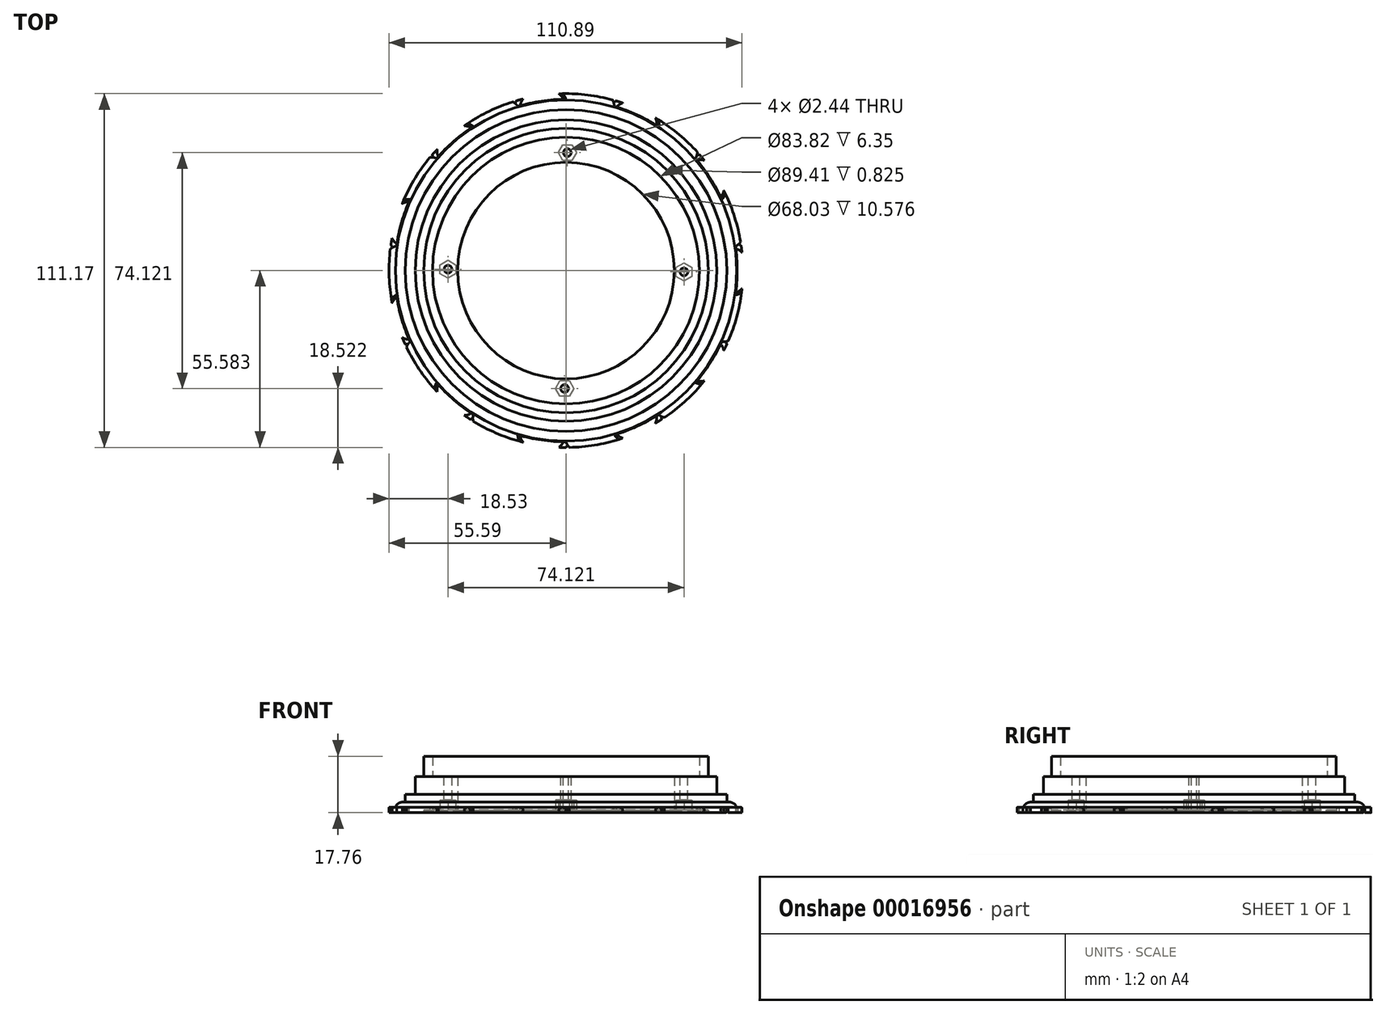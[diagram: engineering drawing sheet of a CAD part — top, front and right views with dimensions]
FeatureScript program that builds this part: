
annotation { "Feature Type Name" : "Feature", "Feature Type Description" : "" }
export const myFeature = defineFeature(function(context is Context, id is Id, definition is map)
    precondition{}
    {
        {
            var Q0;
            Q0=qCreatedBy(makeId("Top.planeOp"),FACE);
            var sketch = newSketch(context, id + "F0", { "sketchPlane" : qUnion([Q0])});
            skCircle(sketch, "E0", {"center": v(0, 0) * mm, "radius": 57.15 * mm, "construction": true});
            skLineSegment(sketch, "E1", {"start": v(0, 0) * mm, "end": v(0, 57.15) * mm, "construction": true});
            skCircle(sketch, "E2", {"center": v(0, 3.34) * mm, "radius": 53.8 * mm});
            skCircle(sketch, "E3", {"center": v(0, 3.34) * mm, "radius": 3.34 * mm, "construction": true});
            skLineSegment(sketch, "E4", {"start": v(0, 3.34) * mm, "end": v(-29.1, 48.6) * mm, "construction": true});
            skLineSegment(sketch, "E5", {"start": v(0, 57.15) * mm, "end": v(-29.1, 48.6) * mm, "construction": true});
            skLineSegment(sketch, "E6", {"start": v(-14.55, 52.88) * mm, "end": v(-29.1, 48.6) * mm, "construction": true});
            skLineSegment(sketch, "E7", {"start": v(-14.02, 24.18) * mm, "end": v(-21.82, 50.74) * mm, "construction": true});
            skCircle(sketch, "E8", {"center": v(-14.55, 52.88) * mm, "radius": 7.58 * mm, "construction": true});
            skLineSegment(sketch, "E9", {"start": v(-15.16, 54.97) * mm, "end": v(-16.68, 60.15) * mm, "construction": true});
            skEllipticalArc(sketch, "E10", {});
            skPoint(sketch, "E11", {"position": v(-15.16, 54.97) * mm});
            skLineSegment(sketch, "E12", {"start": v(-15.16, 54.97) * mm, "end": v(0, 54.97) * mm, "construction": true});
            skPoint(sketch, "E13", {"position": v(-7.58, 54.97) * mm});
            skCircle(sketch, "E14", {"center": v(0, 54.97) * mm, "radius": 7.58 * mm, "construction": true});
            skPoint(sketch, "E15", {"position": v(0, 62.55) * mm});
            skEllipticalArc(sketch, "E16", {});
            skCircle(sketch, "E17", {"center": v(0, 3.34) * mm, "radius": 44.7 * mm});
            skEllipticalArc(sketch, "E18.trimOffspring", {});
            skEllipticalArc(sketch, "E19.trimOffspring", {});
            skLineSegment(sketch, "E20", {"start": v(0, 3.34) * mm, "end": v(-8.33, 61.3) * mm, "construction": true});
            skCircle(sketch, "E21", {"center": v(0, 3.34) * mm, "radius": 55.59 * mm});
            skCircle(sketch, "E22", {"center": v(0, 3.34) * mm, "radius": 127 * mm});
            skLineSegment(sketch, "E23", {"start": v(0, 3.34) * mm, "end": v(-127, 3.34) * mm, "construction": true});
            skLineSegment(sketch, "E24", {"start": v(-53.8, 3.34) * mm, "end": v(-55.59, 3.34) * mm, "construction": true});
            skFitSpline(sketch, "E25.0", {"points": [v(-14.94, 56.45) * mm, v(-15.23, 54.97) * mm, v(-14.94, 53.49) * mm, v(-14.22, 52.3) * mm, v(-13.38, 51.41) * mm, v(-12.35, 50.56) * mm, v(-10.78, 49.6) * mm, v(-8.86, 48.81) * mm, v(-7.15, 48.3) * mm, v(-5.35, 47.87) * mm, v(-3.45, 47.59) * mm, v(-1.5, 47.44) * mm, v(0, 47.4) * mm, v(1.5, 47.44) * mm, v(3.45, 47.59) * mm, v(5.35, 47.87) * mm, v(7.15, 48.3) * mm, v(8.86, 48.81) * mm, v(10.78, 49.6) * mm, v(12.35, 50.56) * mm, v(13.38, 51.41) * mm, v(14.22, 52.3) * mm, v(14.94, 53.49) * mm, v(15.23, 54.97) * mm, v(14.94, 56.45) * mm, v(14.22, 57.63) * mm, v(13.38, 58.53) * mm, v(12.35, 59.38) * mm, v(10.78, 60.34) * mm, v(8.86, 61.13) * mm, v(7.15, 61.64) * mm, v(5.35, 62.07) * mm, v(3.45, 62.35) * mm, v(1.5, 62.5) * mm, v(0, 62.54) * mm, v(-1.5, 62.5) * mm, v(-3.45, 62.35) * mm, v(-5.35, 62.07) * mm, v(-7.15, 61.64) * mm, v(-8.86, 61.13) * mm, v(-10.78, 60.34) * mm, v(-12.35, 59.38) * mm, v(-13.38, 58.53) * mm, v(-14.22, 57.63) * mm, v(-14.94, 56.45) * mm, v(-15.23, 54.97) * mm, v(-14.94, 53.49) * mm]});
            skFitSpline(sketch, "E25.1", {"points": [v(0.2, 55.67) * mm, v(0.07, 57.17) * mm, v(-0.63, 58.5) * mm, v(-1.65, 59.44) * mm, v(-2.71, 60.06) * mm, v(-3.94, 60.6) * mm, v(-5.72, 61.07) * mm, v(-7.78, 61.28) * mm, v(-9.57, 61.3) * mm, v(-11.4, 61.2) * mm, v(-13.31, 60.94) * mm, v(-15.23, 60.52) * mm, v(-16.68, 60.14) * mm, v(-18.1, 59.68) * mm, v(-19.94, 59) * mm, v(-21.68, 58.18) * mm, v(-23.28, 57.27) * mm, v(-24.78, 56.3) * mm, v(-26.4, 55) * mm, v(-27.64, 53.63) * mm, v(-28.38, 52.53) * mm, v(-28.94, 51.43) * mm, v(-29.3, 50.1) * mm, v(-29.16, 48.59) * mm, v(-28.46, 47.25) * mm, v(-27.44, 46.32) * mm, v(-26.38, 45.7) * mm, v(-25.15, 45.17) * mm, v(-23.37, 44.69) * mm, v(-21.31, 44.47) * mm, v(-19.52, 44.46) * mm, v(-17.68, 44.56) * mm, v(-15.78, 44.82) * mm, v(-13.86, 45.23) * mm, v(-12.41, 45.62) * mm, v(-11, 46.08) * mm, v(-9.15, 46.77) * mm, v(-7.41, 47.58) * mm, v(-5.8, 48.5) * mm, v(-4.3, 49.47) * mm, v(-2.7, 50.76) * mm, v(-1.45, 52.12) * mm, v(-0.7, 53.23) * mm, v(-0.15, 54.33) * mm, v(0.2, 55.67) * mm, v(0.07, 57.17) * mm, v(-0.63, 58.5) * mm]});
            skLineSegment(sketch, "E26", {"start": v(0, 57.15) * mm, "end": v(0, 62.7) * mm, "construction": true});
            skPoint(sketch, "E27", {"position": v(0, 57.15) * mm});
            skArc(sketch, "E28", {"start": v(0, 57.15) * mm, "mid": v(-15.16, 54.97) * mm, "end": v(-29.1, 48.6) * mm});
            skArc(sketch, "E29", {"start": v(0, 57.15) * mm, "mid": v(-15.16, 54.97) * mm, "end": v(-29.1, 48.6) * mm, "construction": true});
            skCircle(sketch, "E30", {"center": v(0, 3.34) * mm, "radius": 41.91 * mm});
            const initialGuessF0  = {"E10": [-0.01454519881923172, 0.052879154308840354, 0.9594931524201487, 0.2817319478845903, 0.015159252343327363, 0.007579626171663686, 0, 0.988771500781082], "E16": [0, 0.05497043346980581, -1, 0, 0.015159252343327398, 0.007579626171663695, 1.5707963267948966, 4.71238898038469], "E18.trimOffspring": [0, 0.05497043346980581, -1, 0, 0.015159252343327398, 0.007579626171663695, 5.294413806398706, 0], "E19.trimOffspring": [-0.014545198819231721, 0.05287915430884035, 0.9594931524201485, 0.2817319478845903, 0.015159252343327363, 0.007579626171663686, 1.5707963267948968, 3.141592653589793]};
            skSetInitialGuess(sketch, initialGuessF0);
            skSolve(sketch);
        }
        {
            var Q0;
            Q0=sQuery(id+"F0.wireOp",VERTEX,"E10.start");
            var Q1;
            Q1=sQuery(id+"F0.wireOp",EDGE,"E1");
            cPlane(context, id + "F1", {"entities" : qUnion([Q0, Q1]), "cplaneType" : CPlaneType.LINE_POINT, "offset" : 152.4 * mm, "width" : 152.4 * mm, "height" : 152.4 * mm});
        }
        {
            var Q0;
            Q0=qCreatedBy(id+"F1.planeOp",FACE);
            var sketch = newSketch(context, id + "F2", { "sketchPlane" : qUnion([Q0])});
            skCircle(sketch, "E31", {"center": v(0, 0) * mm, "radius": 0.83 * mm});
            skPoint(sketch, "E31.first.point", {"position": v(-0.82, -0.03) * mm});
            skPoint(sketch, "E31.second.point", {"position": v(0.82, 0.1) * mm});
            skPoint(sketch, "E31.third.point", {"position": v(-0.15, 0.81) * mm});
            skLineSegment(sketch, "E32", {"start": v(-0.82, -0.03) * mm, "end": v(22.8, 0.81) * mm, "construction": true});
            skSolve(sketch);
        }
        {
            var Q0;
            Q0=qSketchRegion(id+"F2",true);
            var Q1;
            Q1=sQuery(id+"F0.wireOp",EDGE,"E10");
            sweep(context, id + "F3", {"profiles" : qUnion([Q0]), "path" : qUnion([Q1])});
        }
        {
            var Q0;
            Q0=sQuery(id+"F0.wireOp",EDGE,"E20");
            cPlane(context, id + "F4", {"entities" : qUnion([Q0]), "cplaneType" : CPlaneType.LINE_ANGLE, "offset" : 152.4 * mm, "angle" : 90 * degree, "width" : 152.4 * mm, "height" : 152.4 * mm});
        }
        {
            var Q0;
            Q0=qCreatedBy(makeId("Right.planeOp"),FACE);
            var sketch = newSketch(context, id + "F5", { "sketchPlane" : qUnion([Q0])});
            skLineSegment(sketch, "E33", {"start": v(3.34, 0) * mm, "end": v(3.34, 43.32) * mm, "construction": true});
            skSolve(sketch);
        }
        {
            var Q0;
            Q0=makeQuery(id+"F3.opSweep","SWEPT_BODY",BODY,{"disambiguationData":[OSD([sQuery(id+"F0.wireOp",EDGE,"E10"),sQuery(id+"F2.wireOp",EDGE,"E31")])]});
            var Q1;
            Q1=qCreatedBy(id+"F4.planeOp",FACE);
            mirror(context, id + "F6", {"operationType" : NewBodyOperationType.ADD, "entities" : qUnion([Q0]), "mirrorPlane" : qUnion([Q1])});
        }
        {
            var Q0;
            {var subQ3=sQuery(id+"F0.wireOp",EDGE,"E2");var subQ5=sQuery(id+"F0.wireOp",EDGE,"E25.1");var subQ7=makeQuery(id+"F0.imprint","INTERSECT",VERTEX,{"derivedFrom":[subQ3,subQ5]});Q0=makeQuery(id+"F0.imprint","IMPRINT",FACE,{"disambiguationData":[TD([[makeQuery(id+"F0.imprint","IMPRINT",EDGE,{"disambiguationData":[TD([[subQ7,-1.0]])],"derivedFrom":subQ3}),-1.0]])]});}
            extrude(context, id + "F7", {"entities" : qUnion([Q0]), "operationType" : NewBodyOperationType.ADD, "endBound" : BoundingType.SYMMETRIC, "depth" : 1.65 * mm});
        }
        {
            var Q0;
            Q0=makeQuery(id+"F3.opSweep","SWEPT_BODY",BODY,{"disambiguationData":[OSD([sQuery(id+"F0.wireOp",EDGE,"E10"),sQuery(id+"F2.wireOp",EDGE,"E31")])]});
            var Q1;
            Q1=sQuery(id+"F5.wireOp",EDGE,"E33");
            circularPattern(context, id + "F8", {"entities" : qUnion([Q0]), "axis" : qUnion([Q1]), "angle" : 32.73 * degree, "instanceCount" : round(11)});
        }
        {
            var Q0;
            Q0=makeQuery(id+"F0.imprint","IMPRINT",FACE,{"disambiguationData":[TD([[makeQuery(id+"F0.imprint","IMPRINT",EDGE,{"derivedFrom":sQuery(id+"F0.wireOp",EDGE,"E17")}),-1.0]])]});
            extrude(context, id + "F9", {"entities" : qUnion([Q0]), "operationType" : NewBodyOperationType.ADD, "endBound" : BoundingType.SYMMETRIC, "depth" : 1.65 * mm});
        }
        {
            var Q0;
            Q0=makeQuery(id+"F0.imprint","IMPRINT",FACE,{"disambiguationData":[TD([[makeQuery(id+"F0.imprint","IMPRINT",EDGE,{"derivedFrom":sQuery(id+"F0.wireOp",EDGE,"E22")}),1.0]])]});
            var Q1;
            {var subQ6=sQuery(id+"F0.wireOp",EDGE,"E18.trimOffspring");var subQ8=sQuery(id+"F0.wireOp",EDGE,"E10");var subQ10=makeQuery(id+"F0.imprint","INTERSECT",VERTEX,{"derivedFrom":[subQ8,subQ6]});Q1=makeQuery(id+"F0.imprint","IMPRINT",FACE,{"disambiguationData":[TD([[makeQuery(id+"F0.imprint","IMPRINT",EDGE,{"disambiguationData":[TD([[subQ10,1.0]])],"derivedFrom":subQ8}),1.0]])]});}
            var Q2;
            {var subQ0=sQuery(id+"F0.wireOp",EDGE,"E25.1");var subQ1=sQuery(id+"F0.wireOp",EDGE,"E21");var subQ2=makeQuery(id+"F0.imprint","INTERSECT",VERTEX,{"derivedFrom":[subQ1,subQ0]});Q2=makeQuery(id+"F0.imprint","IMPRINT",FACE,{"disambiguationData":[TD([[makeQuery(id+"F0.imprint","IMPRINT",EDGE,{"disambiguationData":[TD([[subQ2,-1.0]])],"derivedFrom":subQ1}),-1.0]])]});}
            extrude(context, id + "F10", {"entities" : qUnion([Q0, Q1, Q2]), "operationType" : NewBodyOperationType.REMOVE, "endBound" : BoundingType.SYMMETRIC, "oppositeDirection" : true, "depth" : 25.4 * mm});
        }
        {
            var Q0;
            Q0=qCreatedBy(makeId("Right.planeOp"),FACE);
            var sketch = newSketch(context, id + "F11", { "sketchPlane" : qUnion([Q0])});
            skLineSegment(sketch, "E34", {"start": v(-50.36, 0) * mm, "end": v(-50.36, 0.2) * mm});
            skLineSegment(sketch, "E35", {"start": v(-48.07, 2.48) * mm, "end": v(-47.18, 2.48) * mm});
            skLineSegment(sketch, "E36", {"start": v(-47.18, 2.48) * mm, "end": v(-47.18, 4.94) * mm});
            skLineSegment(sketch, "E37", {"start": v(-47.18, 4.94) * mm, "end": v(-44, 4.94) * mm});
            skLineSegment(sketch, "E38", {"start": v(-44, 4.94) * mm, "end": v(-44, 9.3) * mm});
            skLineSegment(sketch, "E39", {"start": v(-44, 10.58) * mm, "end": v(-30.67, 10.58) * mm});
            skLineSegment(sketch, "E40", {"start": v(-30.67, 10.58) * mm, "end": v(-30.67, 0) * mm});
            skLineSegment(sketch, "E41", {"start": v(-30.67, 0) * mm, "end": v(-50.36, 0) * mm});
            skPoint(sketch, "E42.visualSharp", {"position": v(-50.36, 2.48) * mm});
            skArc(sketch, "E42.filletArc", {"start": v(-48.07, 2.48) * mm, "mid": v(-49.69, 1.8) * mm, "end": v(-50.36, 0.2) * mm});
            skLineSegment(sketch, "E43", {"start": v(-44, 9.3) * mm, "end": v(-48.41, 9.3) * mm, "construction": true});
            skLineSegment(sketch, "E44", {"start": v(-48.41, 9.3) * mm, "end": v(-51.55, 9.3) * mm, "construction": true});
            skLineSegment(sketch, "E45", {"start": v(-44, 9.3) * mm, "end": v(-44, 10.58) * mm});
            skSolve(sketch);
        }
        {
            var Q0;
            Q0=makeQuery(id+"F11.imprint","IMPRINT",FACE,{"disambiguationData":[TD([[makeQuery(id+"F11.imprint","IMPRINT",EDGE,{"derivedFrom":sQuery(id+"F11.wireOp",EDGE,"E34")}),-1.0]])]});
            var Q1;
            Q1=sQuery(id+"F5.wireOp",EDGE,"E33");
            revolve(context, id + "F12", {"operationType" : NewBodyOperationType.ADD, "entities" : qUnion([Q0]), "axis" : qUnion([Q1]), "revolveType" : RevolveType.FULL});
        }
        {
            var Q0;
            Q0=makeQuery(id+"F0.imprint","IMPRINT",FACE,{"disambiguationData":[TD([[makeQuery(id+"F0.imprint","IMPRINT",EDGE,{"derivedFrom":sQuery(id+"F0.wireOp",EDGE,"E17")}),1.0]])]});
            extrude(context, id + "F13", {"entities" : qUnion([Q0]), "depth" : 16.93 * mm, "hasSecondDirection" : true, "secondDirectionOppositeDirection" : false, "secondDirectionDepth" : 10.58 * mm});
        }
        {
            var Q0;
            Q0=makeQuery(id+"F12.opRevolve","SWEPT_FACE",FACE,{"disambiguationData":[OSD([sQuery(id+"F11.wireOp",EDGE,"E39")])]});
            var sketch = newSketch(context, id + "F14", { "sketchPlane" : qUnion([Q0])});
            skLineSegment(sketch, "E46", {"start": v(-34.01, 3.76) * mm, "end": v(-37.06, 3.76) * mm});
            skCircle(sketch, "E47.cCircle", {"center": v(-37.06, 3.76) * mm, "radius": 2.48 * mm, "construction": true});
            skLineSegment(sketch, "E47.0", {"start": v(-37.06, 6.62) * mm, "end": v(-34.58, 5.2) * mm});
            skLineSegment(sketch, "E47.1", {"start": v(-34.58, 5.2) * mm, "end": v(-34.58, 2.33) * mm});
            skLineSegment(sketch, "E47.2", {"start": v(-34.58, 2.33) * mm, "end": v(-37.06, 0.9) * mm});
            skLineSegment(sketch, "E47.3", {"start": v(-37.06, 0.9) * mm, "end": v(-39.54, 2.33) * mm});
            skLineSegment(sketch, "E47.4", {"start": v(-39.54, 2.33) * mm, "end": v(-39.54, 5.2) * mm});
            skLineSegment(sketch, "E47.5", {"start": v(-39.54, 5.2) * mm, "end": v(-37.06, 6.62) * mm});
            skPoint(sketch, "E47.0.midPoint", {"position": v(-35.82, 5.9) * mm});
            skLineSegment(sketch, "E48.1.0", {"start": v(1.01, -36.2) * mm, "end": v(-1.85, -36.2) * mm});
            skLineSegment(sketch, "E48.1.1", {"start": v(2.44, -33.72) * mm, "end": v(1.01, -36.2) * mm});
            skLineSegment(sketch, "E48.1.2", {"start": v(1.01, -31.24) * mm, "end": v(2.44, -33.72) * mm});
            skLineSegment(sketch, "E48.1.3", {"start": v(-1.85, -36.2) * mm, "end": v(-3.28, -33.72) * mm});
            skLineSegment(sketch, "E48.1.4", {"start": v(-3.28, -33.72) * mm, "end": v(-1.85, -31.24) * mm});
            skLineSegment(sketch, "E48.1.5", {"start": v(-1.85, -31.24) * mm, "end": v(1.01, -31.24) * mm});
            skLineSegment(sketch, "E48.2.0", {"start": v(39.54, 4.35) * mm, "end": v(39.54, 1.5) * mm});
            skLineSegment(sketch, "E48.2.1", {"start": v(37.06, 5.78) * mm, "end": v(39.54, 4.35) * mm});
            skLineSegment(sketch, "E48.2.2", {"start": v(34.58, 4.35) * mm, "end": v(37.06, 5.78) * mm});
            skLineSegment(sketch, "E48.2.3", {"start": v(39.54, 1.5) * mm, "end": v(37.06, 0.06) * mm});
            skLineSegment(sketch, "E48.2.4", {"start": v(37.06, 0.06) * mm, "end": v(34.58, 1.5) * mm});
            skLineSegment(sketch, "E48.2.5", {"start": v(34.58, 1.5) * mm, "end": v(34.58, 4.35) * mm});
            skLineSegment(sketch, "E48.3.0", {"start": v(-1.01, 42.88) * mm, "end": v(1.85, 42.88) * mm});
            skLineSegment(sketch, "E48.3.1", {"start": v(-2.44, 40.4) * mm, "end": v(-1.01, 42.88) * mm});
            skLineSegment(sketch, "E48.3.2", {"start": v(-1.01, 37.93) * mm, "end": v(-2.44, 40.4) * mm});
            skLineSegment(sketch, "E48.3.3", {"start": v(1.85, 42.88) * mm, "end": v(3.28, 40.4) * mm});
            skLineSegment(sketch, "E48.3.4", {"start": v(3.28, 40.4) * mm, "end": v(1.85, 37.93) * mm});
            skLineSegment(sketch, "E48.3.5", {"start": v(1.85, 37.93) * mm, "end": v(-1.01, 37.93) * mm});
            skPoint(sketch, "E48.center", {"position": v(0, 3.34) * mm});
            skCircle(sketch, "E49", {"center": v(-37.06, 3.76) * mm, "radius": 1.22 * mm});
            skCircle(sketch, "E50.1.0", {"center": v(-0.42, -33.72) * mm, "radius": 1.22 * mm});
            skCircle(sketch, "E50.2.0", {"center": v(37.06, 2.92) * mm, "radius": 1.22 * mm});
            skCircle(sketch, "E50.3.0", {"center": v(0.42, 40.4) * mm, "radius": 1.22 * mm});
            skPoint(sketch, "E51.0.midPoint", {"position": v(-49.78, 6.28) * mm});
            skSolve(sketch);
        }
        {
            var Q0;
            Q0=makeQuery(id+"F14.imprint","IMPRINT",FACE,{"disambiguationData":[TD([[makeQuery(id+"F14.imprint","IMPRINT",EDGE,{"derivedFrom":sQuery(id+"F14.wireOp",EDGE,"E49")}),1.0]])]});
            var Q1;
            Q1=makeQuery(id+"F14.imprint","IMPRINT",FACE,{"disambiguationData":[TD([[makeQuery(id+"F14.imprint","IMPRINT",EDGE,{"derivedFrom":sQuery(id+"F14.wireOp",EDGE,"E50.3.0")}),1.0]])]});
            var Q2;
            Q2=makeQuery(id+"F14.imprint","IMPRINT",FACE,{"disambiguationData":[TD([[makeQuery(id+"F14.imprint","IMPRINT",EDGE,{"derivedFrom":sQuery(id+"F14.wireOp",EDGE,"E50.2.0")}),1.0]])]});
            var Q3;
            Q3=makeQuery(id+"F14.imprint","IMPRINT",FACE,{"disambiguationData":[TD([[makeQuery(id+"F14.imprint","IMPRINT",EDGE,{"derivedFrom":sQuery(id+"F14.wireOp",EDGE,"E50.1.0")}),1.0]])]});
            extrude(context, id + "F15", {"entities" : qUnion([Q0, Q1, Q2, Q3]), "operationType" : NewBodyOperationType.REMOVE, "endBound" : BoundingType.THROUGH_ALL, "oppositeDirection" : true, "depth" : 25.4 * mm});
        }
        {
            var Q0;
            Q0=makeQuery(id+"F0.imprint","IMPRINT",FACE,{"disambiguationData":[TD([[makeQuery(id+"F0.imprint","IMPRINT",EDGE,{"derivedFrom":sQuery(id+"F0.wireOp",EDGE,"E30")}),1.0]])]});
            var sketch = newSketch(context, id + "F16", { "sketchPlane" : qUnion([Q0])});
            skLineSegment(sketch, "E52.0", {"start": v(-1.01, 37.93) * mm, "end": v(-2.44, 40.4) * mm});
            skLineSegment(sketch, "E52.1", {"start": v(-2.44, 40.4) * mm, "end": v(-1.01, 42.88) * mm});
            skLineSegment(sketch, "E52.2", {"start": v(-1.01, 42.88) * mm, "end": v(1.85, 42.88) * mm});
            skLineSegment(sketch, "E52.3", {"start": v(1.85, 42.88) * mm, "end": v(3.28, 40.4) * mm});
            skLineSegment(sketch, "E52.4", {"start": v(3.28, 40.4) * mm, "end": v(1.85, 37.93) * mm});
            skLineSegment(sketch, "E52.5", {"start": v(1.85, 37.93) * mm, "end": v(-1.01, 37.93) * mm});
            skLineSegment(sketch, "E53.7", {"start": v(-1.85, -36.2) * mm, "end": v(-3.28, -33.72) * mm});
            skLineSegment(sketch, "E53.8", {"start": v(-3.28, -33.72) * mm, "end": v(-1.85, -31.24) * mm});
            skLineSegment(sketch, "E53.9", {"start": v(-1.85, -31.24) * mm, "end": v(1.01, -31.24) * mm});
            skLineSegment(sketch, "E53.10", {"start": v(1.01, -31.24) * mm, "end": v(2.44, -33.72) * mm});
            skLineSegment(sketch, "E53.11", {"start": v(2.44, -33.72) * mm, "end": v(1.01, -36.2) * mm});
            skLineSegment(sketch, "E53.12", {"start": v(1.01, -36.2) * mm, "end": v(-1.85, -36.2) * mm});
            skLineSegment(sketch, "E54.13", {"start": v(-39.54, 5.2) * mm, "end": v(-37.06, 6.62) * mm});
            skLineSegment(sketch, "E54.14", {"start": v(-37.06, 6.62) * mm, "end": v(-34.58, 5.2) * mm});
            skLineSegment(sketch, "E54.15", {"start": v(-34.58, 5.2) * mm, "end": v(-34.58, 2.33) * mm});
            skLineSegment(sketch, "E54.16", {"start": v(-34.58, 2.33) * mm, "end": v(-37.06, 0.9) * mm});
            skLineSegment(sketch, "E54.17", {"start": v(-37.06, 0.9) * mm, "end": v(-39.54, 2.33) * mm});
            skLineSegment(sketch, "E54.18", {"start": v(-39.54, 2.33) * mm, "end": v(-39.54, 5.2) * mm});
            skLineSegment(sketch, "E55.19", {"start": v(34.58, 1.5) * mm, "end": v(34.58, 4.35) * mm});
            skLineSegment(sketch, "E55.20", {"start": v(34.58, 4.35) * mm, "end": v(37.06, 5.78) * mm});
            skLineSegment(sketch, "E55.21", {"start": v(37.06, 5.78) * mm, "end": v(39.54, 4.35) * mm});
            skLineSegment(sketch, "E55.22", {"start": v(39.54, 4.35) * mm, "end": v(39.54, 1.5) * mm});
            skLineSegment(sketch, "E55.23", {"start": v(39.54, 1.5) * mm, "end": v(37.06, 0.06) * mm});
            skLineSegment(sketch, "E55.24", {"start": v(37.06, 0.06) * mm, "end": v(34.58, 1.5) * mm});
            skSolve(sketch);
        }
        {
            var Q0;
            Q0 = qSketchRegion(id + "F16", true);
            extrude(context, id + "F17", {"entities" : qUnion([Q0]), "operationType" : NewBodyOperationType.REMOVE, "depth" : 3.17 * mm});
        }
    });
